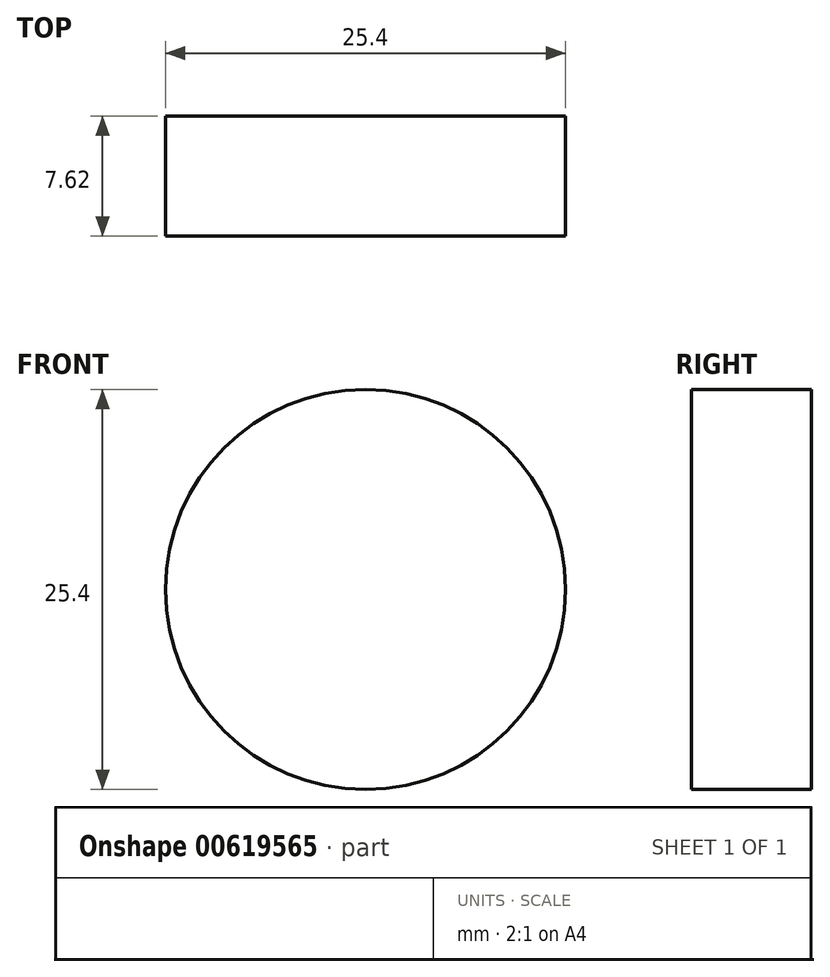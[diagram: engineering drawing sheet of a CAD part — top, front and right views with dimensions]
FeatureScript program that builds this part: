
annotation { "Feature Type Name" : "Feature", "Feature Type Description" : "" }
export const myFeature = defineFeature(function(context is Context, id is Id, definition is map)
    precondition{}
    {
        {
            var Q0;
            Q0=qCreatedBy(makeId("Front.planeOp"),FACE);
            var sketch = newSketch(context, id + "F0", { "sketchPlane" : qUnion([Q0])});
            skCircle(sketch, "E0", {"center": v(0, 0) * mm, "radius": 12.7 * mm});
            skSolve(sketch);
        }
        {
            var Q0;
            Q0 = qSketchRegion(id + "F0", true);
            extrude(context, id + "F1", {"entities" : qUnion([Q0]), "depth" : 7.62 * mm, "offsetDistance" : 25.4 * mm});
        }
        {
            var Q0;
            Q0=makeQuery(id+"F1.opExtrude","CAP_FACE",FACE,{"disambiguationData":[OSD([sQuery(id+"F0.wireOp",EDGE,"E0")])],"isStart":false});
            var sketch = newSketch(context, id + "F2", { "sketchPlane" : qUnion([Q0])});
            skLineSegment(sketch, "E1", {"start": v(0, 0) * mm, "end": v(0, 15.8) * mm, "construction": true});
            skLineSegment(sketch, "E2", {"start": v(-0.5, 15.24) * mm, "end": v(0.5, 15.24) * mm});
            skLineSegment(sketch, "E3", {"start": v(0.5, 15.24) * mm, "end": v(1.32, 12.2) * mm});
            skLineSegment(sketch, "E4", {"start": v(1.32, 12.2) * mm, "end": v(-1.32, 12.2) * mm});
            skLineSegment(sketch, "E5", {"start": v(-1.32, 12.2) * mm, "end": v(-0.5, 15.24) * mm});
            skSolve(sketch);
        }
    });
